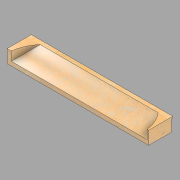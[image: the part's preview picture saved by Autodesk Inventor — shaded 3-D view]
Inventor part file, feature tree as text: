
AUTODESK INVENTOR PART (.ipt)
format: ipt  version: 2022.2 (Build 262287010, 287A)  size: 136,192 bytes
history: native  units: in
note: dims shown in document units (in); Inventor stores cm internally (conversion verified against a paired STEP export)
features: revolve x2, direct_edit x1, other x1
ambient origin geometry x8: Origin, YZ Plane, XZ Plane, XY Plane, X Axis, Y Axis, Z Axis, Center Point
bodies: Solid1 (feature_tree)
feature tree (4):
  direct_edit  "Direct Edit1"
  other  "Head (R)"
  revolve  "Rotate1"  Angle=180.0deg
  revolve  "Rotate2"  [1 undecoded]
note: 1 required parameter value undecoded (feature->parameter linkage not recoverable at this tier; creation-order binding heuristic only, values carry confidence <= 0.55)
